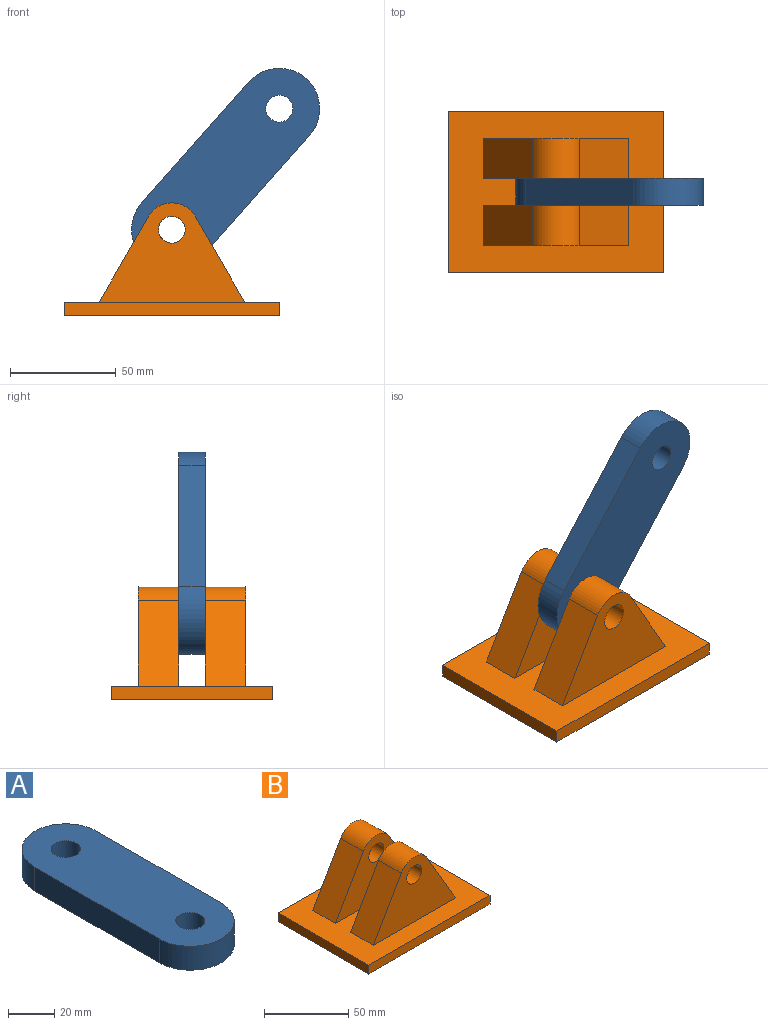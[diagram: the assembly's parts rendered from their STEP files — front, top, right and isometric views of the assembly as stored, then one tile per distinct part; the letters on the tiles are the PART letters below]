
ASSEMBLY  parts=2 mates=1
PART A: 8 faces, bbox 38.1x114.6x12.7 mm
  f0: cylinder r=19.05mm len=38.1mm, axis (0,0,-1), area 760.1mm2, adj f1,f5,f6,f7
  f1: plane 76.47x12.7mm, normal (-1,0,0), area 971.2mm2, adj f0,f2,f6,f7
  f2: cylinder r=19.05mm len=38.1mm, axis (0,0,-1), area 760.1mm2, adj f1,f5,f6,f7
  f3: cylinder r=6.35mm len=12.7mm, axis (0,0,-1), area 506.7mm2, adj f6,f7
  f4: cylinder r=6.35mm len=12.7mm, axis (0,0,-1), area 506.7mm2, adj f6,f7
  f5: plane 76.47x12.7mm, normal (1,0,0), area 971.2mm2, adj f0,f2,f6,f7
  f6: plane 114.57x38.1mm, normal (0,0,1), area 3800.2mm2, adj f0,f1,f2,f3,f4,f5
  f7: plane 114.57x38.1mm, normal (0,0,-1), area 3800.2mm2, adj f0,f1,f2,f3,f4,f5
PART B: 18 faces, bbox 101.6x76.2x53.3 mm
  f0: plane 40.59x23.44mm, normal (0.87,0,0.5), area 892.9mm2, adj f1,f8,f14,f17
  f1: cylinder r=12.7mm len=22mm, axis (0,1,0), area 506.7mm2, adj f0,f2,f14,f17
  f2: plane 40.59x23.44mm, normal (-0.87,0,0.5), area 892.9mm2, adj f1,f8,f14,f17
  f3: cylinder r=6.35mm len=19.05mm, axis (0,1,0), area 760.1mm2, adj f14,f17
  f4: plane 101.6x6.35mm, normal (0,1,0), area 645.2mm2, adj f5,f7,f8,f9
  f5: plane 76.2x6.35mm, normal (-1,0,0), area 483.9mm2, adj f4,f6,f8,f9
  f6: plane 101.6x6.35mm, normal (0,-1,0), area 645.2mm2, adj f5,f7,f8,f9
  f7: plane 76.2x6.35mm, normal (1,0,0), area 483.9mm2, adj f4,f6,f8,f9
  f8: plane 101.6x76.2mm, normal (0,0,1), area 5118.1mm2, adj f0,f2,f4,f5,f6,f7,f10,f12
  f9: plane 101.6x76.2mm, normal (0,0,-1), area 7741.9mm2, adj f4,f5,f6,f7
  f10: plane 40.59x23.44mm, normal (0.87,0,0.5), area 892.9mm2, adj f8,f11,f15,f16
  f11: cylinder r=12.7mm len=22mm, axis (0,1,0), area 506.7mm2, adj f10,f12,f15,f16
  f12: plane 40.59x23.44mm, normal (-0.87,0,0.5), area 892.9mm2, adj f8,f11,f15,f16
  f13: cylinder r=6.35mm len=19.05mm, axis (0,1,0), area 760.1mm2, adj f15,f16
  f14: plane 68.87x46.94mm, normal (0,-1,0), area 1816.5mm2, adj f0,f1,f2,f3,f8
  f15: plane 68.87x46.94mm, normal (0,1,0), area 1816.5mm2, adj f8,f10,f11,f12,f13
  f16: plane 68.87x46.94mm, normal (0,-1,0), area 1816.5mm2, adj f8,f10,f11,f12,f13
  f17: plane 68.87x46.94mm, normal (0,1,0), area 1816.5mm2, adj f0,f1,f2,f3,f8
PLACE A rot(axis=(-0.26,-0.68,-0.68),150.9deg) t=(25.37,-6.35,69.2)mm
PLACE B at identity fixed
MATE revolute B.f3 <-> A.f2  axis (0,-1,0) through (0,6.35,40.59)mm
